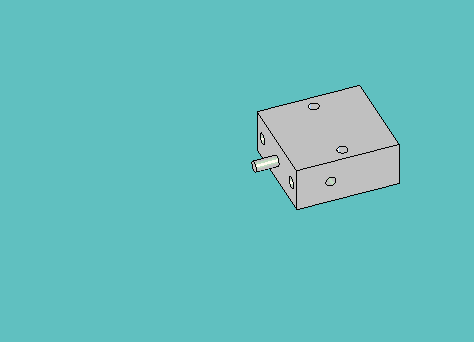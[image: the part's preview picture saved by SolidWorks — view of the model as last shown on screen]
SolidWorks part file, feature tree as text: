
SOLIDWORKS PART (.sldprt)
format: sldprt  version: not decoded by parser v0  size: 337,920 bytes
history: native  units: mm
features: sketch x5, extrude x3, material x1, boolean_combine x1, cut_extrude x1 (+11 scaffold rows collapsed)
feature tree (22):
  scaffold x11  (default folders/planes/origin — collapsed)
  material  "Material <not specified>"
  sketch  "Sketch3"  dims[c1.D2=2.8702mm c1.D4=2.8702mm c1.D1=27.0256mm c2.D2=9.9822mm c2.D3=28.575mm c2.D5=14.2748mm c2.D6=14.2748mm c2.D7=9.906mm c2.D8=9.906mm c2.D9=9.9822mm]
  extrude  "Extrude3"  Depth=6.35mm
  sketch  "Sketch5"  dims[D2=2.9972mm D1=6.35mm]
  extrude  "Extrude4"  Depth=6.35mm
  sketch  "Sketch9"  dims[D1=3.175mm D2=~1.731942mm D3=~6.848039mm D4=~9.921875mm]
  extrude  "Extrude8"  Depth=4.7625mm
  boolean_combine  "Combine5"
  sketch  "Sketch10"
  sketch  "Sketch14"  dims[D2=~2.778125mm D1=9.525mm]
  cut_extrude  "Cut-Extrude2"  [1 undecoded]
decode coverage: 7 of 10 modeling features carry decoded parameters
note: ~ marks probable driven/reference dimensions
note: 1 parameter value undecoded
note: suppression state not decoded; provenance and decode notes live in map.json
